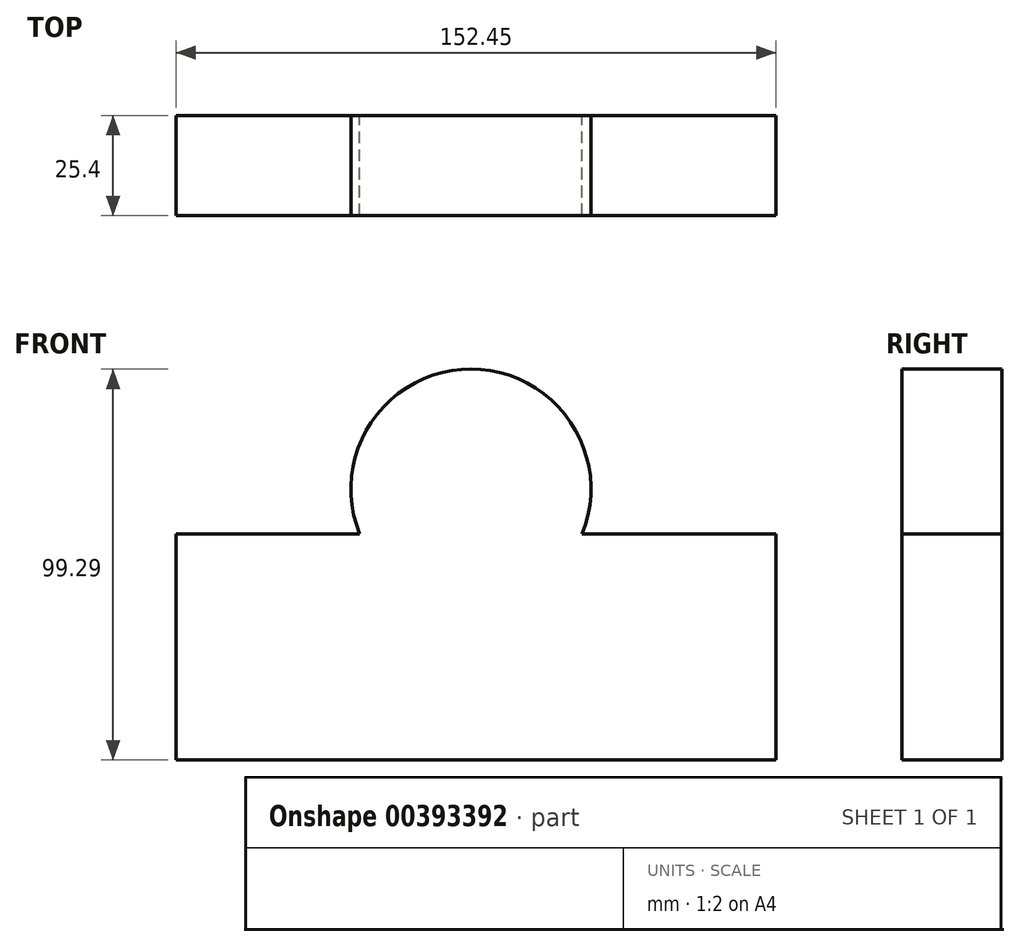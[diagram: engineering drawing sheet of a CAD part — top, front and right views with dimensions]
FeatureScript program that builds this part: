
annotation { "Feature Type Name" : "Feature", "Feature Type Description" : "" }
export const myFeature = defineFeature(function(context is Context, id is Id, definition is map)
    precondition{}
    {
        {
            var Q0;
            Q0=qCreatedBy(makeId("Front.planeOp"),FACE);
            var sketch = newSketch(context, id + "F0", { "sketchPlane" : qUnion([Q0])});
            skLineSegment(sketch, "E0.bottom", {"start": v(-76.37, -25.5) * mm, "end": v(76.08, -25.5) * mm});
            skLineSegment(sketch, "E0.left", {"start": v(-76.37, -25.5) * mm, "end": v(-76.37, 31.92) * mm});
            skLineSegment(sketch, "E0.right", {"start": v(76.08, -25.5) * mm, "end": v(76.08, 31.92) * mm});
            skArc(sketch, "E1", {"start": v(26.82, 31.92) * mm, "mid": v(-1.46, 73.79) * mm, "end": v(-29.73, 31.92) * mm});
            skLineSegment(sketch, "E2", {"start": v(-76.37, 31.92) * mm, "end": v(-29.73, 31.92) * mm});
            skLineSegment(sketch, "E3", {"start": v(26.82, 31.92) * mm, "end": v(76.08, 31.92) * mm});
            skSolve(sketch);
        }
        {
            var Q0;
            Q0 = qSketchRegion(id + "F0", true);
            extrude(context, id + "F1", {"entities" : qUnion([Q0]), "depth" : 25.4 * mm});
        }
    });
